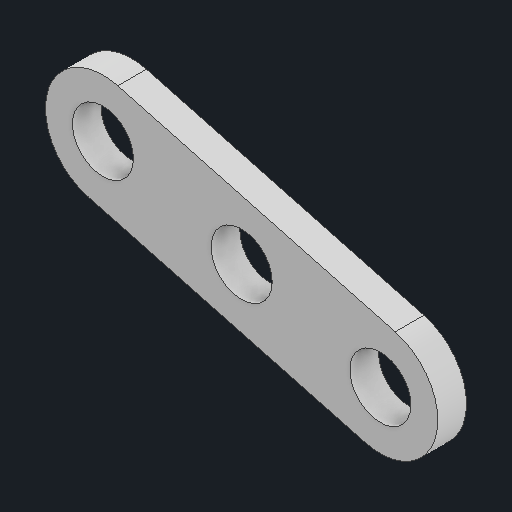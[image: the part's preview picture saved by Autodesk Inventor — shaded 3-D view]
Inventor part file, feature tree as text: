
AUTODESK INVENTOR PART (.ipt)
format: ipt  version: 2023 (Build 270158000, 158)  size: 145,920 bytes
history: native  units: in
note: dims shown in document units (in); Inventor stores cm internally (conversion verified against a paired STEP export)
features: other x4, reference x3, sketch x2, plane x1, extrude x1, hole x1
ambient origin geometry x8: Origin, YZ Plane, XZ Plane, XY Plane, X Axis, Y Axis, Z Axis, Center Point
bodies: Solid1 (feature_tree)
feature tree (12):
  plane  "Work Plane1"
  extrude  "Extrusion1"  Depth=0.5in
  hole  "Hole1"  [1 undecoded]
  sketch  "Sketch1"  dims[d0=0.625in d1=0.5in]
  reference  "Reference1"
  reference  "Reference2"
  reference  "Reference3"
  sketch  "Sketch2"  dims[d2=0.125in d3=0.0in d4=0.266in d5=0.75in d6=0.507in d7=0.25in d8=0.5635in d9=0.536in d10=0.0in]
  other  "<userpath>\Desktop\WaccaController\Wacca Controller\Touch Segment\Touch Segment.iam"
  other  "Touch Segment.iam"
  other  "Front Plate:1"
  other  "<userpath>\Desktop\Wacca Controller V3\Touch Segment\Touch Segment.iam"
note: 1 required parameter value undecoded (feature->parameter linkage not recoverable at this tier; creation-order binding heuristic only, values carry confidence <= 0.55)
